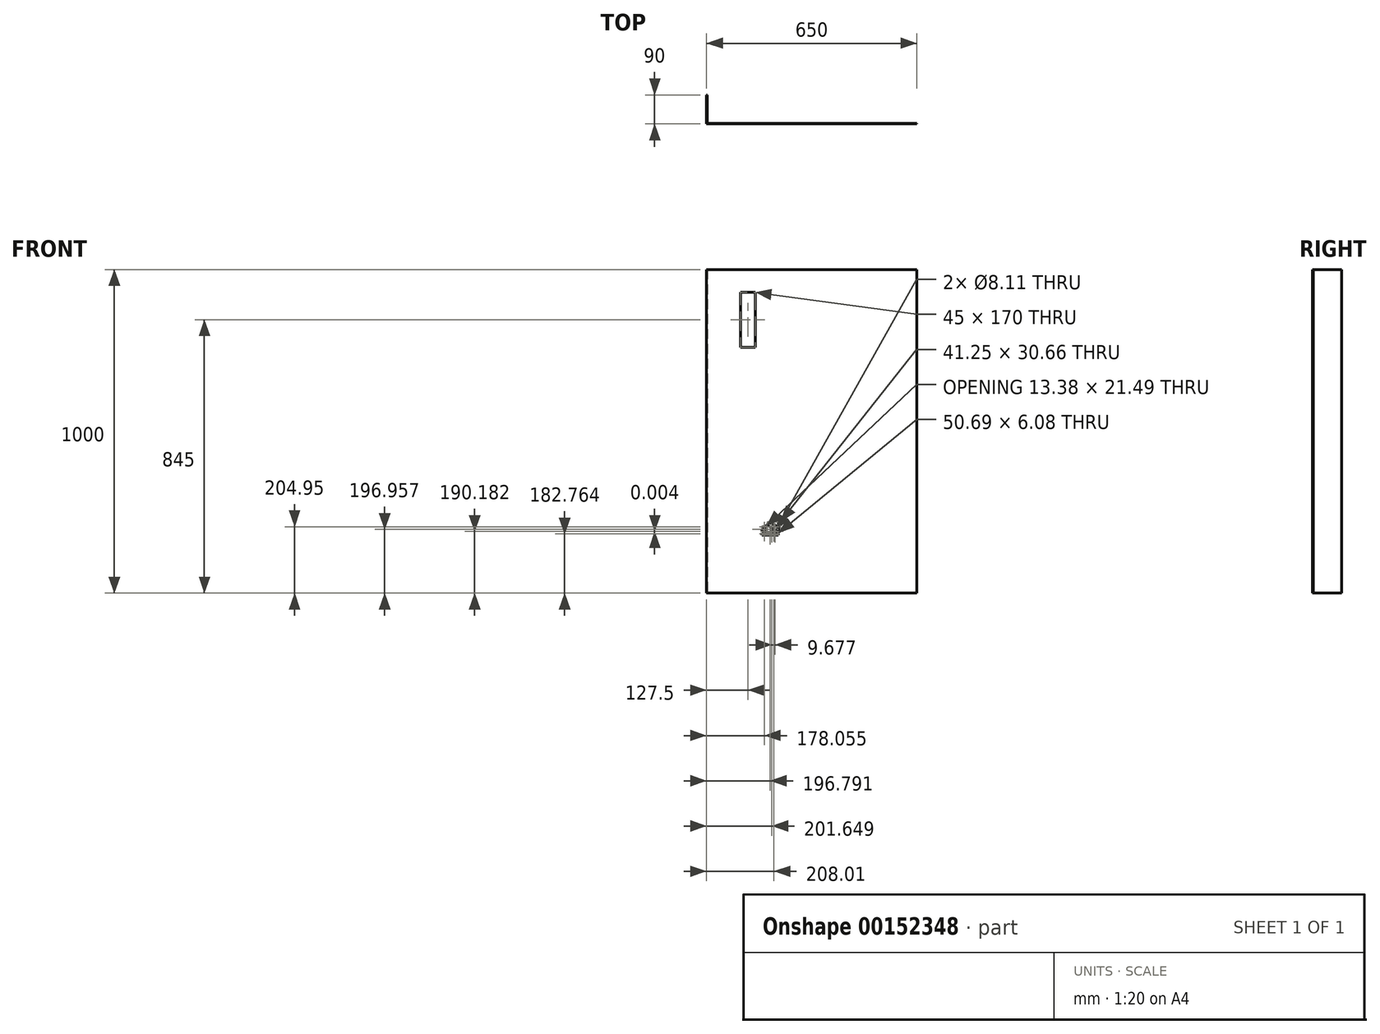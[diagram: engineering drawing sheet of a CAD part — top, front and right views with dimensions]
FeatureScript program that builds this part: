
annotation { "Feature Type Name" : "Feature", "Feature Type Description" : "" }
export const myFeature = defineFeature(function(context is Context, id is Id, definition is map)
    precondition{}
    {
        {
            var Q0;
            Q0=qCreatedBy(makeId("Front.planeOp"),FACE);
            var sketch = newSketch(context, id + "F0", { "sketchPlane" : qUnion([Q0])});
            skLineSegment(sketch, "E0.bottom", {"start": v(-200, 800) * mm, "end": v(450, 800) * mm});
            skLineSegment(sketch, "E0.top", {"start": v(-200, -200) * mm, "end": v(450, -200) * mm});
            skLineSegment(sketch, "E0.left", {"start": v(-200, 800) * mm, "end": v(-200, -200) * mm});
            skLineSegment(sketch, "E0.right", {"start": v(450, 800) * mm, "end": v(450, -200) * mm});
            skLineSegment(sketch, "E1", {"start": v(-198, 800) * mm, "end": v(-198, -200) * mm});
            skLineSegment(sketch, "E2.bottom", {"start": v(-95, 730) * mm, "end": v(-50, 730) * mm});
            skLineSegment(sketch, "E2.top", {"start": v(-95, 560) * mm, "end": v(-50, 560) * mm});
            skLineSegment(sketch, "E2.left", {"start": v(-95, 730) * mm, "end": v(-95, 560) * mm});
            skLineSegment(sketch, "E2.right", {"start": v(-50, 730) * mm, "end": v(-50, 560) * mm});
            skLineSegment(sketch, "E3", {"start": v(-12.62, 9.7) * mm, "end": v(22.6, -10.38) * mm});
            skLineSegment(sketch, "E4", {"start": v(22.6, -10.38) * mm, "end": v(28.64, 0.19) * mm});
            skLineSegment(sketch, "E5", {"start": v(28.64, 0.19) * mm, "end": v(-6.59, 20.28) * mm});
            skLineSegment(sketch, "E6", {"start": v(-6.59, 20.28) * mm, "end": v(-12.62, 9.7) * mm});
            skLineSegment(sketch, "E7", {"start": v(-28.64, -1.02) * mm, "end": v(-28.64, -9.73) * mm});
            skLineSegment(sketch, "E8", {"start": v(-28.64, -9.73) * mm, "end": v(-24.78, -9.73) * mm});
            skLineSegment(sketch, "E9", {"start": v(-16.67, -9.73) * mm, "end": v(-15.25, -9.73) * mm});
            skLineSegment(sketch, "E10", {"start": v(-15.25, -9.73) * mm, "end": v(-15.25, 3.65) * mm});
            skArc(sketch, "E11", {"start": v(-15.25, 3.65) * mm, "mid": v(-16.44, 6.51) * mm, "end": v(-19.3, 7.7) * mm});
            skLineSegment(sketch, "E12", {"start": v(-19.3, 7.7) * mm, "end": v(-23.36, 7.7) * mm});
            skArc(sketch, "E13", {"start": v(-24.78, -9.73) * mm, "mid": v(-20.73, -13.79) * mm, "end": v(-16.67, -9.73) * mm});
            skCircle(sketch, "E14", {"center": v(11.33, -9.81) * mm, "radius": 4.06 * mm});
            skCircle(sketch, "E15", {"center": v(1.65, -9.82) * mm, "radius": 4.06 * mm});
            skLineSegment(sketch, "E16", {"start": v(-23.36, 7.7) * mm, "end": v(-28.64, -1.02) * mm});
            skLineSegment(sketch, "E17", {"start": v(-28.55, -20.28) * mm, "end": v(22.14, -20.28) * mm});
            skLineSegment(sketch, "E18", {"start": v(22.14, -20.28) * mm, "end": v(22.14, -14.2) * mm});
            skLineSegment(sketch, "E19", {"start": v(22.14, -14.2) * mm, "end": v(-28.55, -14.2) * mm});
            skLineSegment(sketch, "E20", {"start": v(-28.55, -14.2) * mm, "end": v(-28.55, -20.28) * mm});
            skSolve(sketch);
        }
        {
            var Q0;
            {var subQ0=sQuery(id+"F0.wireOp",EDGE,"E0.left");Q0=makeQuery(id+"F0.imprint","IMPRINT",FACE,{"disambiguationData":[TD([[makeQuery(id+"F0.imprint","IMPRINT",EDGE,{"derivedFrom":subQ0}),1.0]])]});}
            extrude(context, id + "F1", {"entities" : qUnion([Q0]), "oppositeDirection" : true, "depth" : 90 * mm});
        }
        {
            var Q0;
            {var subQ1=sQuery(id+"F0.wireOp",EDGE,"E0.right");Q0=makeQuery(id+"F0.imprint","IMPRINT",FACE,{"disambiguationData":[TD([[makeQuery(id+"F0.imprint","IMPRINT",EDGE,{"derivedFrom":subQ1}),-1.0]])]});}
            extrude(context, id + "F2", {"entities" : qUnion([Q0]), "operationType" : NewBodyOperationType.ADD, "oppositeDirection" : true, "depth" : 2 * mm});
        }
    });
